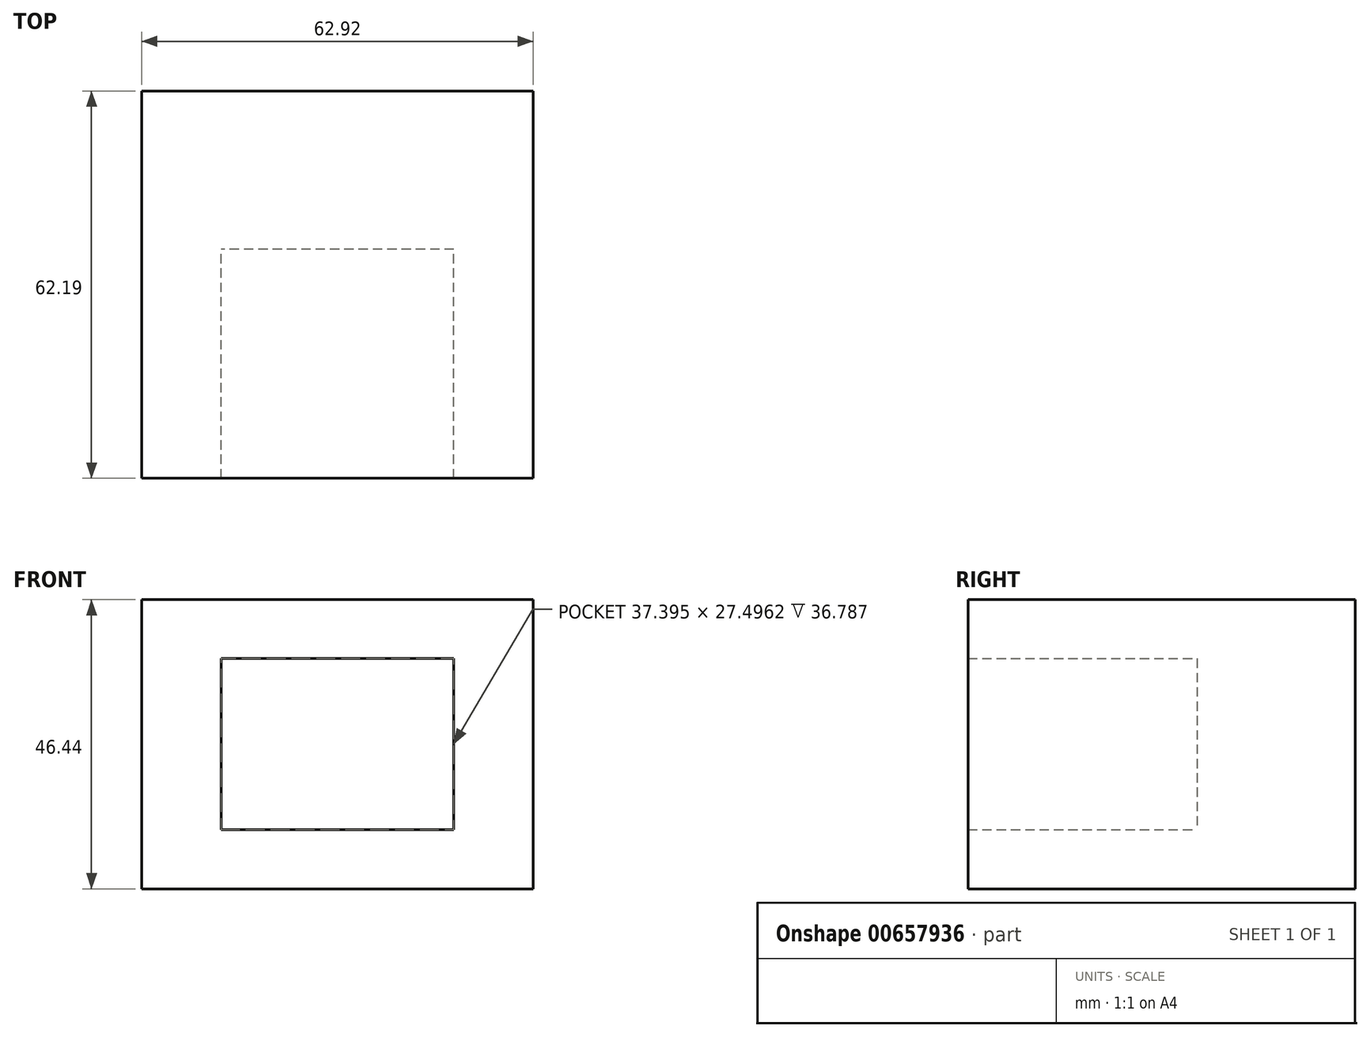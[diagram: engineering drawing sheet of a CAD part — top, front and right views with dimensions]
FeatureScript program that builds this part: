
annotation { "Feature Type Name" : "Feature", "Feature Type Description" : "" }
export const myFeature = defineFeature(function(context is Context, id is Id, definition is map)
    precondition{}
    {
        {
            var Q0;
            Q0=qCreatedBy(makeId("Front.planeOp"),FACE);
            var sketch = newSketch(context, id + "F0", { "sketchPlane" : qUnion([Q0])});
            skLineSegment(sketch, "E0.bottom", {"start": v(18.7, 13.75) * mm, "end": v(-18.7, 13.75) * mm});
            skLineSegment(sketch, "E0.top", {"start": v(18.7, -13.75) * mm, "end": v(-18.7, -13.75) * mm});
            skLineSegment(sketch, "E0.left", {"start": v(18.7, 13.75) * mm, "end": v(18.7, -13.75) * mm});
            skLineSegment(sketch, "E0.right", {"start": v(-18.7, 13.75) * mm, "end": v(-18.7, -13.75) * mm});
            skPoint(sketch, "E0.middle", {"position": v(0, 0) * mm});
            skLineSegment(sketch, "E1.bottom", {"start": v(31.46, 23.22) * mm, "end": v(-31.46, 23.22) * mm});
            skLineSegment(sketch, "E1.top", {"start": v(31.46, -23.22) * mm, "end": v(-31.46, -23.22) * mm});
            skLineSegment(sketch, "E1.left", {"start": v(31.46, 23.22) * mm, "end": v(31.46, -23.22) * mm});
            skLineSegment(sketch, "E1.right", {"start": v(-31.46, 23.22) * mm, "end": v(-31.46, -23.22) * mm});
            skSolve(sketch);
        }
        {
            var Q0;
            Q0=makeQuery(id+"F0.imprint","IMPRINT",FACE,{"disambiguationData":[TD([[makeQuery(id+"F0.imprint","IMPRINT",EDGE,{"derivedFrom":sQuery(id+"F0.wireOp",EDGE,"E0.bottom")}),-1.0]])]});
            extrude(context, id + "F1", {"entities" : qUnion([Q0]), "depth" : 62.19 * mm, "offsetDistance" : 25.4 * mm});
        }
        {
            var Q0;
            Q0=qCreatedBy(makeId("Front.planeOp"),FACE);
            var sketch = newSketch(context, id + "F2", { "sketchPlane" : qUnion([Q0])});
            skLineSegment(sketch, "E2.bottom", {"start": v(-18.83, 13.81) * mm, "end": v(18.83, 13.81) * mm});
            skLineSegment(sketch, "E2.top", {"start": v(-18.83, -13.81) * mm, "end": v(18.83, -13.81) * mm});
            skLineSegment(sketch, "E2.left", {"start": v(-18.83, 13.81) * mm, "end": v(-18.83, -13.81) * mm});
            skLineSegment(sketch, "E2.right", {"start": v(18.83, 13.81) * mm, "end": v(18.83, -13.81) * mm});
            skPoint(sketch, "E2.middle", {"position": v(0, 0) * mm});
            skSolve(sketch);
        }
        {
            var Q0;
            Q0=makeQuery(id+"F2.imprint","IMPRINT",FACE,{"disambiguationData":[TD([[makeQuery(id+"F2.imprint","IMPRINT",EDGE,{"derivedFrom":sQuery(id+"F2.wireOp",EDGE,"E2.bottom")}),-1.0]])]});
            extrude(context, id + "F3", {"entities" : qUnion([Q0]), "operationType" : NewBodyOperationType.ADD, "depth" : 25.4 * mm, "offsetDistance" : 25.4 * mm});
        }
    });
